# Revit family: Waste_Floor_Nero_Square
name_source: partatom
category: Plumbing Fixtures
units: mm (PartAtom-declared; Revit-internal decimal feet)

## family parameters
Always vertical = Yes
Cut with Voids When Loaded = Yes
Maintain Annotation Orientation = No
OmniClass Number = 23.31.00.00
Part Type = Normal
Room Calculation Point = No
Round Connector Dimension = Use Diameter
Shared = No
Work Plane-Based = No

## types (20) — shared parameters
Assembly Code = C1030210
CW Connection = Yes
HW Connection = Yes
Manufacturer = Nero
ManufacturerURLProductSpecific = https://nerotapware.com.au
URL = https://nerotapware.com.au
Uniclass2015Code = Pr_65_52_24_28
Uniclass2015Title = Floor channels
Uniclass2015Version = Products v1.35
Vent Connection = No
Waste Connection = No
zero-valued in all types: Default Elevation

## per-type parameters (varying)
| type | BodyMaterial | Description | IfcExportAs | IfcExportType | InnerGrateDepth | InnerGrateWidth | ManufacturerOverallDepth | ManufacturerOverallHeight | ManufacturerOverallWidth | ManufacturerSpecCode | Model | ModifiedIssue | OutletDiameter | Type Comments |
| Brushed Bronze (NRFW008BZ) | Metal_Bronze_Nero_Brushed | 130mm Square Tile Insert Floor Waste 100mm Outlet Brushed Bronze | IfcWasteTerminal | WASTE TRAP | 113 mm | 113 mm | 126 mm | 42 mm | 126 mm | NRFW008BZ | NRFW008BZ | 20240428 $ | 103 mm | Waste - Floor - Brushed Bronze |
| Gun Metal (NRFW008GM) | Metal_GunMetal_Nero | 130mm Square Tile Insert Floor Waste 100mm Outlet Gun Metal | IfcWasteTerminal | WASTE TRAP | 113 mm | 113 mm | 126 mm | 42 mm | 126 mm | NRFW008GM | NRFW008GM | 20240428 $ | 103 mm | Waste - Floor - Gun Metal |
| Brushed Gold (NRFW008BG) | Metal_Gold_Nero_Brushed | 130mm Square Tile Insert Floor Waste 100mm Outlet Brushed Gold | IfcWasteTerminal | WASTE TRAP | 113 mm | 113 mm | 126 mm | 42 mm | 126 mm | NRFW008BG | NRFW008BG | 20240428 $ | 103 mm | Waste - Floor - Brushed Gold |
| Brushed Nickel (NRFW008BN) | Metal_Nickel_Nero_Brushed | 130mm Square Tile Insert Floor Waste 100mm Outlet Brushed Nickel | IfcWasteTerminal | WASTE TRAP | 113 mm | 113 mm | 126 mm | 42 mm | 126 mm | NRFW008BN | NRFW008BN | 20240428 $ | 103 mm | Waste - Floor - Brushed Nickel |
| Matte Black (NRFW008MB) | Metal_MatteBlack_Nero | 130mm Square Tile Insert Floor Waste 100mm Outlet Matte Black | IfcWasteTerminal | WASTE TRAP | 113 mm | 113 mm | 126 mm | 42 mm | 126 mm | NRFW008MB | NRFW008MB | 20240428 $ | 103 mm | Waste - Floor - Matte Black |
| Brushed Bronze (NRFW007BZ) | Metal_Bronze_Nero_Brushed | 130mm Square Tile Insert Floor Waste 80mm Outlet Brushed Bronze | IfcWasteTerminal | WASTE TRAP | 113 mm | 113 mm | 126 mm | 43.5 mm | 126 mm | NRFW007BZ | NRFW007BZ | 20240428 $ | 75 mm | Waste - Floor - Brushed Bronze |
| Gun Metal (NRFW007GM) | Metal_GunMetal_Nero | 130mm Square Tile Insert Floor Waste 80mm Outlet Gun Metal | IfcWasteTerminal | WASTE TRAP | 113 mm | 113 mm | 126 mm | 43.5 mm | 126 mm | NRFW007GM | NRFW007GM | 20240428 $ | 75 mm | Waste - Floor - Gun Metal |
| Brushed Gold (NRFW007BG) | Metal_Gold_Nero_Brushed | 130mm Square Tile Insert Floor Waste 80mm Outlet Brushed Gold | IfcWasteTerminal | WASTE TRAP | 113 mm | 113 mm | 126 mm | 43.5 mm | 126 mm | NRFW007BG | NRFW007BG | 20240428 $ | 75 mm | Waste - Floor - Brushed Gold |
| Brushed Nickel (NRFW007BN) | Metal_Nickel_Nero_Brushed | 130mm Square Tile Insert Floor Waste 80mm Outlet Brushed Nickel | IfcWasteTerminal | WASTE TRAP | 113 mm | 113 mm | 126 mm | 43.5 mm | 126 mm | NRFW007BN | NRFW007BN | 20240428 $ | 75 mm | Waste - Floor - Brushed Nickel |
| Matte Black (NRFW007MB) | Metal_MatteBlack_Nero | 130mm Square Tile Insert Floor Waste 80mm Outlet Matte Black | IfcWasteTerminal | WASTE TRAP | 113 mm | 113 mm | 126 mm | 43.5 mm | 126 mm | NRFW007MB | NRFW007MB | 20240428 $ | 75 mm | Waste - Floor - Matte Black |
| Brushed Bronze (NRFW006BZ) | Metal_Bronze_Nero_Brushed | 100mm Square Tile Insert Floor Waste 50mm Outlet Brushed Bronze | IfcWasteTerminal | WASTE TRAP | 88 mm  [stored 0.288714 ft] | 88 mm  [stored 0.288714 ft] | 100 mm  [stored 0.328084 ft] | 44 mm  [stored 0.144357 ft] | 100 mm  [stored 0.328084 ft] | NRFW006BZ | NRFW006BZ | 20240428 $ | 50 mm  [stored 0.164042 ft] | Waste - Floor - Brushed Bronze |
| Gun Metal (NRFW006GM) | Metal_GunMetal_Nero | 100mm Square Tile Insert Floor Waste 50mm Outlet Gun Metal | IfcWasteTerminal | WASTE TRAP | 88 mm  [stored 0.288714 ft] | 88 mm  [stored 0.288714 ft] | 100 mm  [stored 0.328084 ft] | 44 mm  [stored 0.144357 ft] | 100 mm  [stored 0.328084 ft] | NRFW006GM | NRFW006GM | 20240428 $ | 50 mm  [stored 0.164042 ft] | Waste - Floor - Gun Metal |
| Brushed Gold (NRFW006BG) | Metal_Gold_Nero_Brushed | 100mm Square Tile Insert Floor Waste 50mm Outlet Brushed Gold | IfcWasteTerminal | WASTE TRAP | 88 mm  [stored 0.288714 ft] | 88 mm  [stored 0.288714 ft] | 100 mm  [stored 0.328084 ft] | 44 mm  [stored 0.144357 ft] | 100 mm  [stored 0.328084 ft] | NRFW006BG | NRFW006BG | 20240428 $ | 50 mm  [stored 0.164042 ft] | Waste - Floor - Brushed Gold |
| Brushed Nickel (NRFW006BN) | Metal_Nickel_Nero_Brushed | 100mm Square Tile Insert Floor Waste 50mm Outlet Brushed Nickel | IfcWasteTerminal | WASTE TRAP | 88 mm  [stored 0.288714 ft] | 88 mm  [stored 0.288714 ft] | 100 mm  [stored 0.328084 ft] | 44 mm  [stored 0.144357 ft] | 100 mm  [stored 0.328084 ft] | NRFW006BN | NRFW006BN | 20240428 $ | 50 mm  [stored 0.164042 ft] | Waste - Floor - Brushed Nickel |
| Matte Black (NRFW006MB) | Metal_MatteBlack_Nero | 100mm Square Tile Insert Floor Waste 50mm Outlet Matte Black | IfcWasteTerminal | WASTE TRAP | 88 mm  [stored 0.288714 ft] | 88 mm  [stored 0.288714 ft] | 100 mm  [stored 0.328084 ft] | 44 mm  [stored 0.144357 ft] | 100 mm  [stored 0.328084 ft] | NRFW006MB | NRFW006MB | 20240428 $ | 50 mm  [stored 0.164042 ft] | Waste - Floor - Matte Black |
| Matte Black (NRFW009MB) | Metal_MatteBlack_Nero | 100mm Square Tile Insert Floor Waste 80mm Outlet Matte Black | IfcSanitaryTerminal | NOTDEFINED | 88 mm  [stored 0.288714 ft] | 88 mm  [stored 0.288714 ft] | 100 mm  [stored 0.328084 ft] | 44 mm  [stored 0.144357 ft] | 100 mm  [stored 0.328084 ft] | NRFW009MB | NRFW009MB | 20250123 $ | 76 mm | Drain - Floor - Square - Matte Black |
| Gun Metal (NRFW009GM) | Metal_GunMetal_Nero | 100mm Square Tile Insert Floor Waste 80mm Outlet Gun Metal | IfcSanitaryTerminal | NOTDEFINED | 88 mm  [stored 0.288714 ft] | 88 mm  [stored 0.288714 ft] | 100 mm  [stored 0.328084 ft] | 44 mm  [stored 0.144357 ft] | 100 mm  [stored 0.328084 ft] | NRFW009GM | NRFW009GM | 20250123 $ | 76 mm | Drain - Floor - Square - Gun Metal |
| Brushed Bronze (NRFW009BZ) | Metal_Bronze_Nero_Brushed | 100mm Square Tile Insert Floor Waste 80mm Outlet Brushed Bronze | IfcSanitaryTerminal | NOTDEFINED | 88 mm  [stored 0.288714 ft] | 88 mm  [stored 0.288714 ft] | 100 mm  [stored 0.328084 ft] | 44 mm  [stored 0.144357 ft] | 100 mm  [stored 0.328084 ft] | NRFW009BZ | NRFW009BZ | 20250123 $ | 76 mm | Drain - Floor - Square - Brushed Bronze |
| Brushed Nickel (NRFW009BN) | Metal_Nickel_Nero_Brushed | 100mm Square Tile Insert Floor Waste 80mm Outlet Brushed Nickel | IfcSanitaryTerminal | NOTDEFINED | 88 mm  [stored 0.288714 ft] | 88 mm  [stored 0.288714 ft] | 100 mm  [stored 0.328084 ft] | 44 mm  [stored 0.144357 ft] | 100 mm  [stored 0.328084 ft] | NRFW009BN | NRFW009BN | 20250123 $ | 76 mm | Drain - Floor - Square - Brushed Nickel |
| Brushed Gold (NRFW009BG) | Metal_Gold_Nero_Brushed | 100mm Square Tile Insert Floor Waste 80mm Outlet Brushed Gold | IfcSanitaryTerminal | NOTDEFINED | 88 mm  [stored 0.288714 ft] | 88 mm  [stored 0.288714 ft] | 100 mm  [stored 0.328084 ft] | 44 mm  [stored 0.144357 ft] | 100 mm  [stored 0.328084 ft] | NRFW009BG | NRFW009BG | 20250123 $ | 76 mm | Drain - Floor - Square - Brushed Gold |

note: [stored X ft] marks values corroborated as IEEE doubles in the binary element streams (Revit-internal decimal feet)

## geometry (parser evidence)
native form markers: Sweep x3
no freeform markers — native parametric forms only
